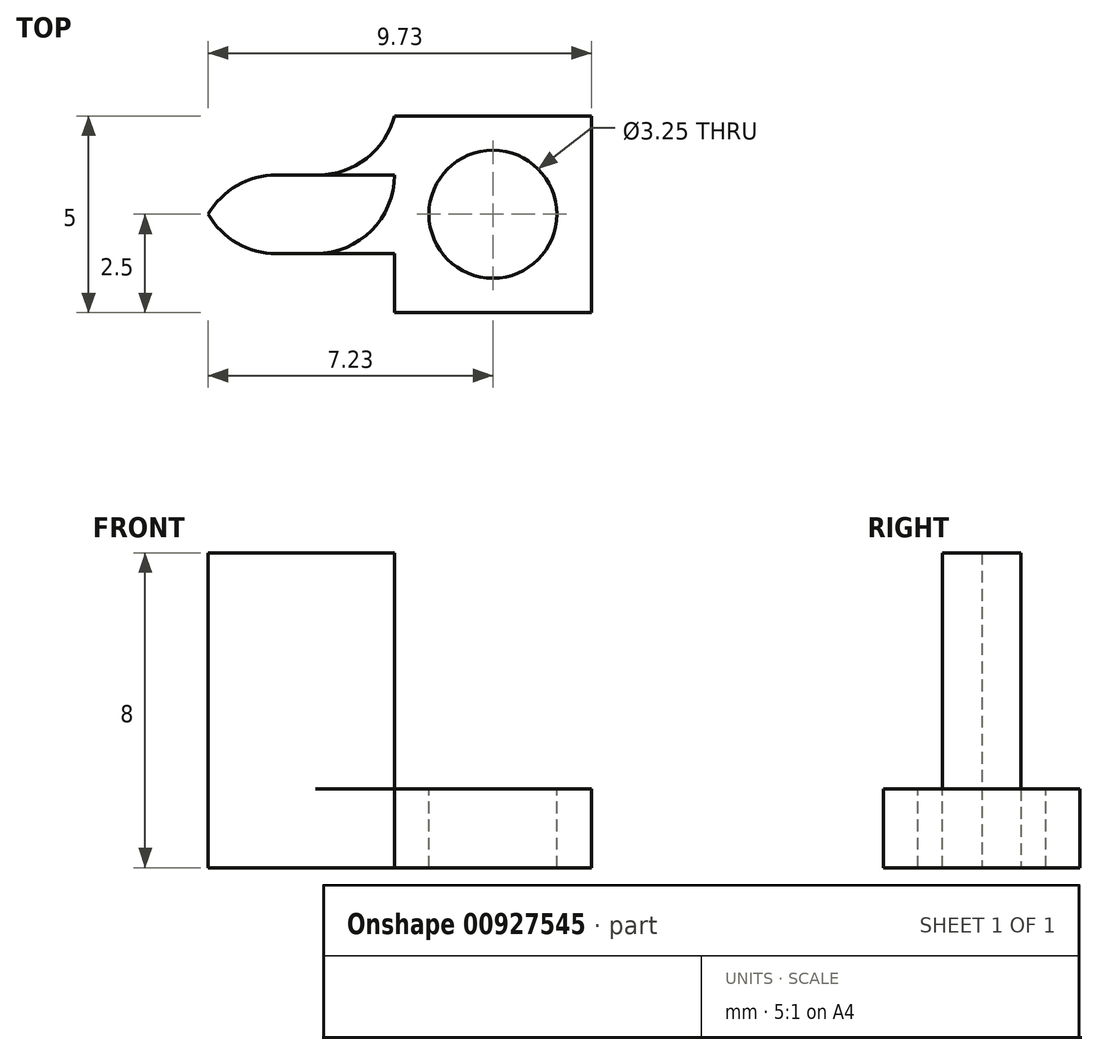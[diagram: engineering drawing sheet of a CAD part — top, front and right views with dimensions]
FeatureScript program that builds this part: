
annotation { "Feature Type Name" : "Feature", "Feature Type Description" : "" }
export const myFeature = defineFeature(function(context is Context, id is Id, definition is map)
    precondition{}
    {
        {
            var Q0;
            Q0=qCreatedBy(makeId("Right.planeOp"),FACE);
            var sketch = newSketch(context, id + "F0", { "sketchPlane" : qUnion([Q0])});
            skLineSegment(sketch, "E0.bottom", {"start": v(0, 0) * mm, "end": v(2, 0) * mm});
            skLineSegment(sketch, "E0.top", {"start": v(0, 8) * mm, "end": v(2, 8) * mm});
            skLineSegment(sketch, "E0.left", {"start": v(0, 0) * mm, "end": v(0, 8) * mm});
            skLineSegment(sketch, "E0.right", {"start": v(2, 0) * mm, "end": v(2, 8) * mm});
            skSolve(sketch);
        }
        {
            var Q0;
            Q0=makeQuery(id+"F0.imprint","IMPRINT",FACE,{"disambiguationData":[TD([[makeQuery(id+"F0.imprint","IMPRINT",EDGE,{"derivedFrom":sQuery(id+"F0.wireOp",EDGE,"E0.bottom")}),1.0]])]});
            extrude(context, id + "F1", {"entities" : qUnion([Q0]), "oppositeDirection" : true, "depth" : 5 * mm, "offsetDistance" : 25 * mm});
        }
        {
            var Q0;
            Q0=makeQuery(id+"F1.opExtrude","CAP_FACE",FACE,{"disambiguationData":[OSD([sQuery(id+"F0.wireOp",EDGE,"E0.bottom"),sQuery(id+"F0.wireOp",EDGE,"E0.top"),sQuery(id+"F0.wireOp",EDGE,"E0.left"),sQuery(id+"F0.wireOp",EDGE,"E0.right")])],"isStart":true});
            var sketch = newSketch(context, id + "F2", { "sketchPlane" : qUnion([Q0])});
            skLineSegment(sketch, "E1.bottom", {"start": v(-1.5, 2) * mm, "end": v(3.5, 2) * mm});
            skLineSegment(sketch, "E1.top", {"start": v(-1.5, 0) * mm, "end": v(3.5, 0) * mm});
            skLineSegment(sketch, "E1.left", {"start": v(-1.5, 2) * mm, "end": v(-1.5, 0) * mm});
            skLineSegment(sketch, "E1.right", {"start": v(3.5, 2) * mm, "end": v(3.5, 0) * mm});
            skPoint(sketch, "E2", {"position": v(1, 0) * mm});
            skSolve(sketch);
        }
        {
            var Q0;
            Q0 = qSketchRegion(id + "F2", true);
            extrude(context, id + "F3", {"entities" : qUnion([Q0]), "operationType" : NewBodyOperationType.ADD, "depth" : 5 * mm, "offsetDistance" : 25 * mm});
        }
        {
            var Q0;
            {var subQ0=sQuery(id+"F0.wireOp",EDGE,"E0.right");Q0=makeQuery(id+"F3.boolean.opBoolean","SPLIT",EDGE,{"disambiguationData":[topologyDisambiguationEdgeConnected([makeQuery(id+"F3.opExtrude","CAP_FACE",FACE,{"disambiguationData":[OSD([sQuery(id+"F2.wireOp",EDGE,"E1.bottom"),sQuery(id+"F2.wireOp",EDGE,"E1.top"),sQuery(id+"F2.wireOp",EDGE,"E1.left"),sQuery(id+"F2.wireOp",EDGE,"E1.right")])],"isStart":true})])],"derivedFrom":makeQuery(id+"F1.opExtrude","CAP_EDGE",EDGE,{"disambiguationData":[OSD([subQ0])],"isStart":true})});}
            var Q1;
            {var subQ0=sQuery(id+"F0.wireOp",EDGE,"E0.left");Q1=makeQuery(id+"F3.boolean.opBoolean","SPLIT",EDGE,{"disambiguationData":[topologyDisambiguationEdgeConnected([makeQuery(id+"F3.opExtrude","CAP_FACE",FACE,{"disambiguationData":[OSD([sQuery(id+"F2.wireOp",EDGE,"E1.bottom"),sQuery(id+"F2.wireOp",EDGE,"E1.top"),sQuery(id+"F2.wireOp",EDGE,"E1.left"),sQuery(id+"F2.wireOp",EDGE,"E1.right")])],"isStart":true})])],"derivedFrom":makeQuery(id+"F1.opExtrude","CAP_EDGE",EDGE,{"disambiguationData":[OSD([subQ0])],"isStart":true})});}
            fillet(context, id + "F4", {"entities" : qUnion([Q0, Q1]), "radius" : 2 * mm, "tangentPropagation" : true, "allowEdgeOverflow" : false});
        }
        {
            var Q0;
            Q0=qCreatedBy(makeId("Right.planeOp"),FACE);
            cPlane(context, id + "F5", {"entities" : qUnion([Q0]), "cplaneType" : CPlaneType.OFFSET, "offset" : 2.5 * mm, "oppositeDirection" : true, "width" : 150 * mm, "height" : 150 * mm});
        }
        {
            var Q0;
            {var subQ0=sQuery(id+"F0.wireOp",EDGE,"E0.right");Q0=makeQuery(id+"FWXJhOhvEBQrtyI_1.1.F3.boolean.opBoolean","SPLIT",EDGE,{"disambiguationData":[topologyDisambiguationEdgeConnected([makeQuery(id+"FWXJhOhvEBQrtyI_1.1.F3.opExtrude","CAP_FACE",FACE,{"disambiguationData":[OSD([sQuery(id+"F2.wireOp",EDGE,"E1.bottom"),sQuery(id+"F2.wireOp",EDGE,"E1.top"),sQuery(id+"F2.wireOp",EDGE,"E1.left"),sQuery(id+"F2.wireOp",EDGE,"E1.right")])],"isStart":true})])],"derivedFrom":makeQuery(id+"F1.opExtrude","CAP_EDGE",EDGE,{"disambiguationData":[OSD([subQ0])],"isStart":false})});}
            var Q1;
            {var subQ0=sQuery(id+"F0.wireOp",EDGE,"E0.left");Q1=makeQuery(id+"FWXJhOhvEBQrtyI_1.1.F3.boolean.opBoolean","SPLIT",EDGE,{"disambiguationData":[topologyDisambiguationEdgeConnected([makeQuery(id+"FWXJhOhvEBQrtyI_1.1.F3.opExtrude","CAP_FACE",FACE,{"disambiguationData":[OSD([sQuery(id+"F2.wireOp",EDGE,"E1.bottom"),sQuery(id+"F2.wireOp",EDGE,"E1.top"),sQuery(id+"F2.wireOp",EDGE,"E1.left"),sQuery(id+"F2.wireOp",EDGE,"E1.right")])],"isStart":true})])],"derivedFrom":makeQuery(id+"F1.opExtrude","CAP_EDGE",EDGE,{"disambiguationData":[OSD([subQ0])],"isStart":false})});}
            fillet(context, id + "F6", {"entities" : qUnion([Q0, Q1]), "radius" : 2 * mm, "tangentPropagation" : true, "allowEdgeOverflow" : false});
        }
        {
            var Q0;
            Q0=makeQuery(id+"F3.opExtrude","SWEPT_FACE",FACE,{"disambiguationData":[OSD([sQuery(id+"F2.wireOp",EDGE,"E1.bottom")])]});
            var sketch = newSketch(context, id + "F7", { "sketchPlane" : qUnion([Q0])});
            skCircle(sketch, "E3", {"center": v(2.5, 1) * mm, "radius": 1.62 * mm});
            skSolve(sketch);
        }
        {
            var Q0;
            Q0 = qSketchRegion(id + "F7", true);
            extrude(context, id + "F8", {"entities" : qUnion([Q0]), "operationType" : NewBodyOperationType.REMOVE, "endBound" : BoundingType.THROUGH_ALL, "oppositeDirection" : true, "depth" : 25 * mm, "offsetDistance" : 25 * mm});
        }
    });
